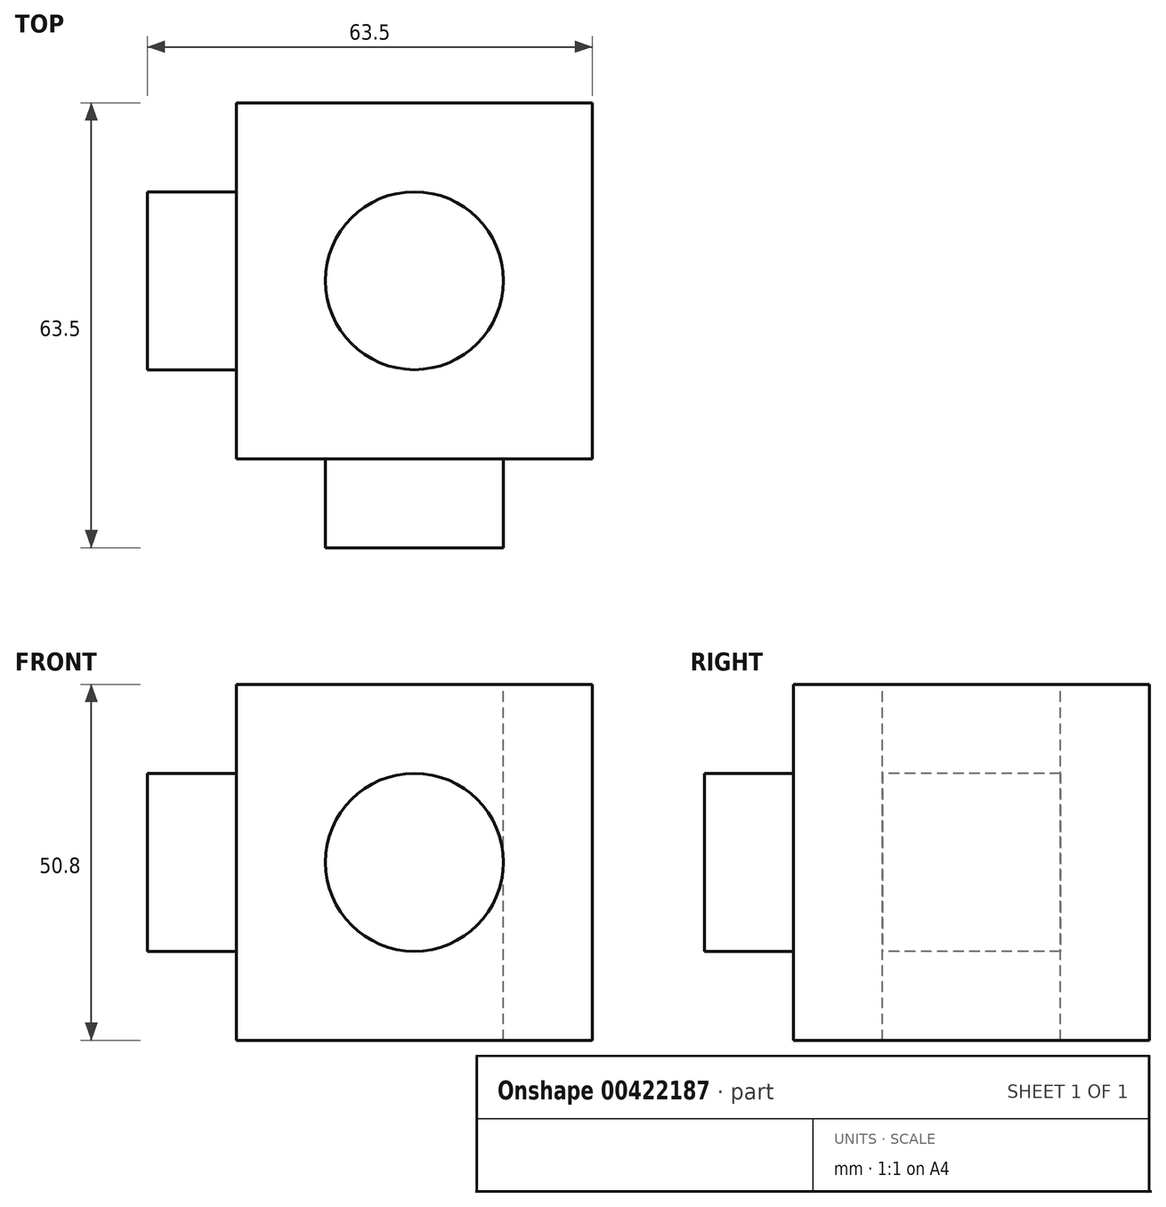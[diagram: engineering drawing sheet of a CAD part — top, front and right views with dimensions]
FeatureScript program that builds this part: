
annotation { "Feature Type Name" : "Feature", "Feature Type Description" : "" }
export const myFeature = defineFeature(function(context is Context, id is Id, definition is map)
    precondition{}
    {
        {
            var Q0;
            Q0=qCreatedBy(makeId("Front.planeOp"),FACE);
            var sketch = newSketch(context, id + "F0", { "sketchPlane" : qUnion([Q0])});
            skLineSegment(sketch, "E0.bottom", {"start": v(-27.12, 30.37) * mm, "end": v(23.68, 30.37) * mm});
            skLineSegment(sketch, "E0.top", {"start": v(-27.12, -20.43) * mm, "end": v(23.68, -20.43) * mm});
            skLineSegment(sketch, "E0.left", {"start": v(-27.12, 30.37) * mm, "end": v(-27.12, -20.43) * mm});
            skLineSegment(sketch, "E0.right", {"start": v(23.68, 30.37) * mm, "end": v(23.68, -20.43) * mm});
            skSolve(sketch);
        }
        {
            var Q0;
            Q0 = qSketchRegion(id + "F0", true);
            extrude(context, id + "F1", {"entities" : qUnion([Q0]), "depth" : 50.8 * mm});
        }
        {
            var Q0;
            Q0=makeQuery(id+"F1.opExtrude","CAP_FACE",FACE,{"disambiguationData":[OSD([sQuery(id+"F0.wireOp",EDGE,"E0.bottom"),sQuery(id+"F0.wireOp",EDGE,"E0.top"),sQuery(id+"F0.wireOp",EDGE,"E0.left"),sQuery(id+"F0.wireOp",EDGE,"E0.right")])],"isStart":false});
            var sketch = newSketch(context, id + "F2", { "sketchPlane" : qUnion([Q0])});
            skCircle(sketch, "E1", {"center": v(-1.72, 4.97) * mm, "radius": 12.7 * mm});
            skSolve(sketch);
        }
        {
            var Q0;
            Q0=makeQuery(id+"F2.imprint","IMPRINT",FACE,{"disambiguationData":[TD([[makeQuery(id+"F2.imprint","IMPRINT",EDGE,{"derivedFrom":sQuery(id+"F2.wireOp",EDGE,"E1")}),1.0]])]});
            extrude(context, id + "F3", {"entities" : qUnion([Q0]), "operationType" : NewBodyOperationType.ADD, "depth" : 12.7 * mm});
        }
        {
            var Q0;
            Q0=makeQuery(id+"F1.opExtrude","SWEPT_FACE",FACE,{"disambiguationData":[OSD([sQuery(id+"F0.wireOp",EDGE,"E0.left")])]});
            var sketch = newSketch(context, id + "F4", { "sketchPlane" : qUnion([Q0])});
            skLineSegment(sketch, "E2.bottom", {"start": v(12.7, 17.67) * mm, "end": v(38.1, 17.67) * mm});
            skLineSegment(sketch, "E2.top", {"start": v(12.7, -7.73) * mm, "end": v(38.1, -7.73) * mm});
            skLineSegment(sketch, "E2.left", {"start": v(12.7, 17.67) * mm, "end": v(12.7, -7.73) * mm});
            skLineSegment(sketch, "E2.right", {"start": v(38.1, 17.67) * mm, "end": v(38.1, -7.73) * mm});
            skSolve(sketch);
        }
        {
            var Q0;
            Q0=makeQuery(id+"F4.imprint","IMPRINT",FACE,{"disambiguationData":[TD([[makeQuery(id+"F4.imprint","IMPRINT",EDGE,{"derivedFrom":sQuery(id+"F4.wireOp",EDGE,"E2.bottom")}),-1.0]])]});
            extrude(context, id + "F5", {"entities" : qUnion([Q0]), "operationType" : NewBodyOperationType.ADD, "depth" : 12.7 * mm});
        }
        {
            var Q0;
            Q0=makeQuery(id+"F1.opExtrude","SWEPT_FACE",FACE,{"disambiguationData":[OSD([sQuery(id+"F0.wireOp",EDGE,"E0.bottom")])]});
            var sketch = newSketch(context, id + "F6", { "sketchPlane" : qUnion([Q0])});
            skCircle(sketch, "E3", {"center": v(-1.72, -25.4) * mm, "radius": 12.7 * mm});
            skSolve(sketch);
        }
        {
            var Q0;
            Q0=makeQuery(id+"F6.imprint","IMPRINT",FACE,{"disambiguationData":[TD([[makeQuery(id+"F6.imprint","IMPRINT",EDGE,{"derivedFrom":sQuery(id+"F6.wireOp",EDGE,"E3")}),1.0]])]});
            extrude(context, id + "F7", {"entities" : qUnion([Q0]), "operationType" : NewBodyOperationType.REMOVE, "oppositeDirection" : true, "depth" : 50.8 * mm});
        }
    });
